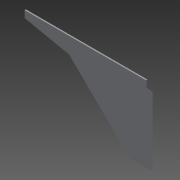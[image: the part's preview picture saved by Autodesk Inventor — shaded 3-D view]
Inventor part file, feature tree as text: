
AUTODESK INVENTOR PART (.ipt)
format: ipt  version: 2014 SP1 (Build 180222100, 222)  size: 151,552 bytes
history: native  units: mm
features: sketch x4, plane x3, loft x2, extrude x1, other x1
ambient origin geometry x8: Origin, YZ Plane, XZ Plane, XY Plane, X Axis, Y Axis, Z Axis, Center Point
bodies: Solid1 (feature_tree)
feature tree (11):
  sketch  "Sketch1"  dims[d0=-35.0mm d1=-220.0mm]
  plane  "Work Plane1"
  sketch  "Sketch2"  dims[d2=85.0mm d3=0.0mm d4=90.0deg]
  plane  "Work Plane2"
  loft  "Loft1"
  loft  "Loft2"
  plane  "Work Plane3"
  extrude  "Extrusion1"  TaperAngle=0.0deg  [1 undecoded]
  sketch  "Sketch3"  dims[d5=0.0mm d6=90.0deg d7=0.0mm d8=90.0deg]
  other  "Edges1"
  sketch  "Sketch4"  dims[d9=0.0mm d10=90.0deg d11=0.0mm d12=450.0mm d13=5.0mm d14=450.0mm d15=25.0mm d16=0.0mm]
note: 1 required parameter value undecoded (feature->parameter linkage not recoverable at this tier; creation-order binding heuristic only, values carry confidence <= 0.55)
